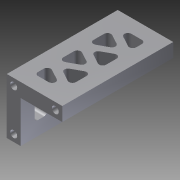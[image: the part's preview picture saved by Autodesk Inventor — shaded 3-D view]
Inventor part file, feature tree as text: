
AUTODESK INVENTOR PART (.ipt)
format: ipt  version: 2012 (Build 160160000, 160)  size: 300,032 bytes
history: native  units: in
note: dims shown in document units (in); Inventor stores cm internally (conversion verified against a paired STEP export)
features: extrude x5, sketch x4, fillet x4, projected_geometry x2, hole x1, plane x1
ambient origin geometry x8: Origin, YZ Plane, XZ Plane, XY Plane, X Axis, Y Axis, Z Axis, Center Point
bodies: Solid1 (feature_tree)
feature tree (17):
  sketch  "Sketch1"  dims[d0=1.0in d1=1.0in]
  extrude  "Extrusion1"  Depth=1.0in
  hole  "Hole1"  [1 undecoded]
  plane  "Work Plane1"
  sketch  "Sketch2"  dims[d2=0.5in d3=0.5in]
  extrude  "Extrusion2"  Depth=0.25in
  extrude  "Extrusion3"  Depth=0.125in
  extrude  "Extrusion4"  Depth=0.125in
  fillet  "Fillet1"  Radius=0.125in
  fillet  "Fillet2"  Radius=0.125in
  fillet  "Fillet3"  Radius=0.125in
  fillet  "Fillet4"  Radius=0.125in
  extrude  "Extrusion5"  Depth=2.0in TaperAngle=0.0deg
  sketch  "Sketch3"  dims[d4=0.25in d5=0.25in]
  projected_geometry  "Projected Loop1"
  projected_geometry  "Projected Loop2"
  sketch  "Sketch4"  dims[d6=0.75in d7=0.125in d8=0.125in d9=0.125in d10=0.125in d11=0.125in d12=0.125in d13=2.0in d14=0.0in d15=0.125in d16=0.75in d17=0.375in d18=0.25in d19=0.5635in d20=0.375in d21=0.8108in d22=-0.125in d23=0.375in d24=0.0in d26=0.5in d27=0.25in d28=0.25in d30=0.0625in d31=0.125in d32=0.0625in d33=0.125in d34=0.0625in d36=0.125in d37=0.0625in d38=0.125in d39=0.0625in d40=0.125in d45=0.1959in d48=0.3918in d49=0.3918in d50=0.3918in d51=0.3918in d52=0.375in d53=0.0in d55=0.5in d56=0.25in d57=0.25in d58=0.0625in d59=0.125in d60=0.0625in d61=0.125in d62=0.0625in d63=0.125in d64=0.0625in d65=0.125in d66=0.0625in d67=0.125in d68=0.1959in d69=0.3918in d70=0.3918in d71=0.3918in d72=0.3918in d73=0.25in d74=3.28in d75=0.375in d76=0.0in d77=0.25in d78=0.25in d83=0.0625in d84=0.0625in d85=0.0625in d86=0.0625in d87=1.0in d88=0.0in]
note: 1 required parameter value undecoded (feature->parameter linkage not recoverable at this tier; creation-order binding heuristic only, values carry confidence <= 0.55)
